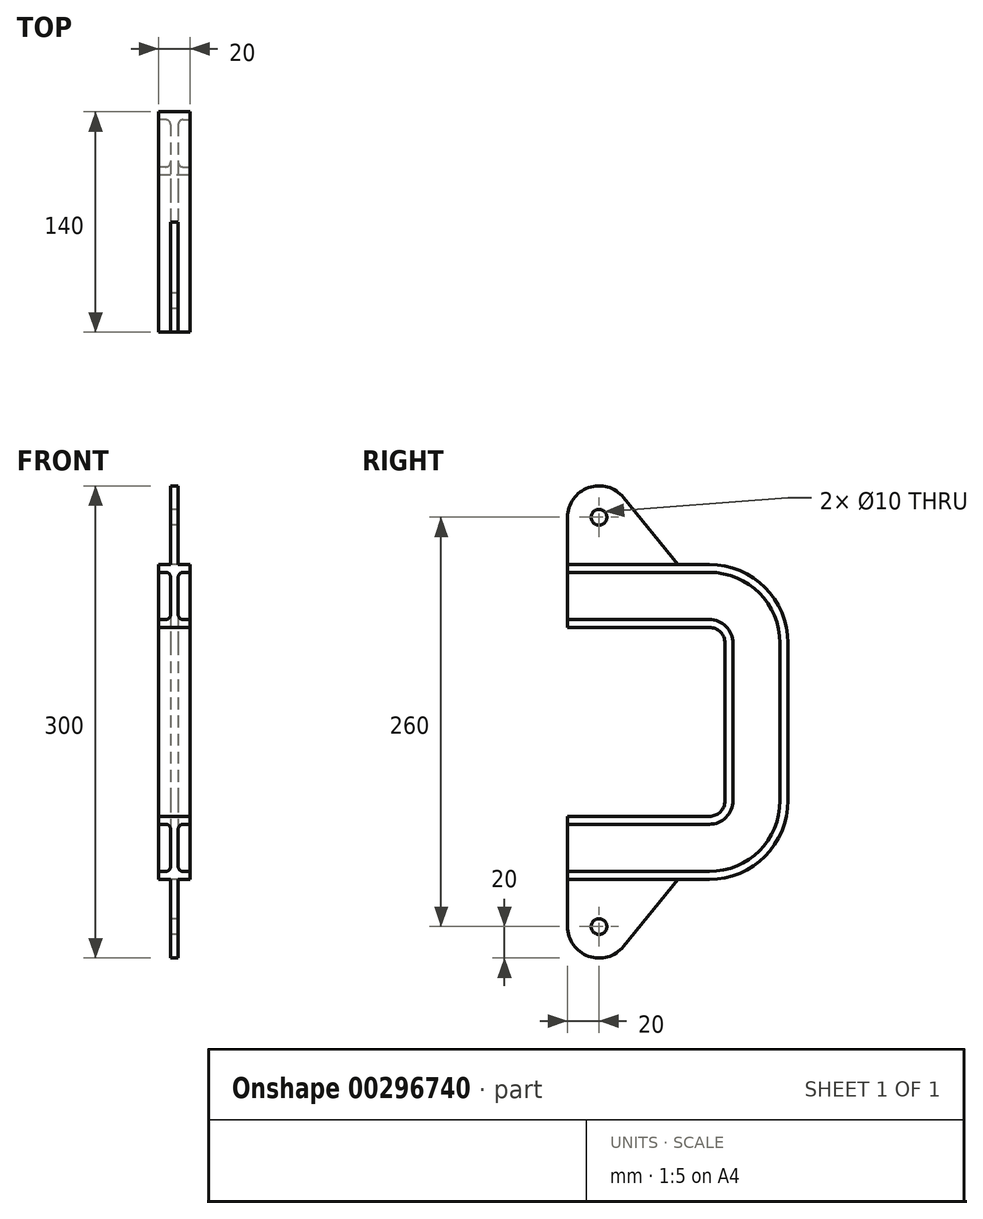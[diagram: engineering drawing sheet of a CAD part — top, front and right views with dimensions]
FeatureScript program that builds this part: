
annotation { "Feature Type Name" : "Feature", "Feature Type Description" : "" }
export const myFeature = defineFeature(function(context is Context, id is Id, definition is map)
    precondition{}
    {
        {
            var Q0;
            Q0=qCreatedBy(makeId("Front.planeOp"),FACE);
            var sketch = newSketch(context, id + "F0", { "sketchPlane" : qUnion([Q0])});
            skLineSegment(sketch, "E0", {"start": v(2.5, 0) * mm, "end": v(2.5, 12) * mm});
            skLineSegment(sketch, "E1", {"start": v(5.5, 15) * mm, "end": v(10, 15) * mm});
            skLineSegment(sketch, "E2", {"start": v(10, 15) * mm, "end": v(10, 20) * mm});
            skLineSegment(sketch, "E3", {"start": v(10, 20) * mm, "end": v(0, 20) * mm});
            skLineSegment(sketch, "E4.MirrorCS", {"start": v(-10, 15) * mm, "end": v(-10, 20) * mm});
            skLineSegment(sketch, "E5.MirrorCS", {"start": v(-5.5, 15) * mm, "end": v(-10, 15) * mm});
            skLineSegment(sketch, "E6.MirrorCS", {"start": v(-2.5, 0) * mm, "end": v(-2.5, 12) * mm});
            skLineSegment(sketch, "E7.MirrorCS", {"start": v(-10, 20) * mm, "end": v(0, 20) * mm});
            skLineSegment(sketch, "E8.MirrorCS", {"start": v(-10, -20) * mm, "end": v(0, -20) * mm});
            skLineSegment(sketch, "E9.MirrorCS", {"start": v(-2.5, 0) * mm, "end": v(-2.5, -12) * mm});
            skLineSegment(sketch, "E10.MirrorCS", {"start": v(5.5, -15) * mm, "end": v(10, -15) * mm});
            skLineSegment(sketch, "E11.MirrorCS", {"start": v(-10, -15) * mm, "end": v(-10, -20) * mm});
            skLineSegment(sketch, "E12.MirrorCS", {"start": v(2.5, 0) * mm, "end": v(2.5, -12) * mm});
            skLineSegment(sketch, "E13.MirrorCS", {"start": v(-5.5, -15) * mm, "end": v(-10, -15) * mm});
            skLineSegment(sketch, "E14.MirrorCS", {"start": v(10, -20) * mm, "end": v(0, -20) * mm});
            skLineSegment(sketch, "E15.MirrorCS", {"start": v(10, -15) * mm, "end": v(10, -20) * mm});
            skPoint(sketch, "E16.visualSharp", {"position": v(2.5, 15) * mm});
            skArc(sketch, "E16.filletArc", {"start": v(5.5, 15) * mm, "mid": v(3.38, 14.12) * mm, "end": v(2.5, 12) * mm});
            skPoint(sketch, "E17.visualSharp", {"position": v(-2.5, 15) * mm});
            skArc(sketch, "E17.filletArc", {"start": v(-2.5, 12) * mm, "mid": v(-3.38, 14.12) * mm, "end": v(-5.5, 15) * mm});
            skPoint(sketch, "E18.visualSharp", {"position": v(-2.5, -15) * mm});
            skArc(sketch, "E18.filletArc", {"start": v(-5.5, -15) * mm, "mid": v(-3.38, -14.12) * mm, "end": v(-2.5, -12) * mm});
            skPoint(sketch, "E19.visualSharp", {"position": v(2.5, -15) * mm});
            skArc(sketch, "E19.filletArc", {"start": v(2.5, -12) * mm, "mid": v(3.38, -14.12) * mm, "end": v(5.5, -15) * mm});
            skSolve(sketch);
        }
        {
            var Q0;
            Q0=qCreatedBy(makeId("Right.planeOp"),FACE);
            var sketch = newSketch(context, id + "F1", { "sketchPlane" : qUnion([Q0])});
            skLineSegment(sketch, "E20", {"start": v(0, -20) * mm, "end": v(90, -20) * mm});
            skLineSegment(sketch, "E21", {"start": v(100, -30) * mm, "end": v(100, -80) * mm});
            skPoint(sketch, "E22.visualSharp", {"position": v(100, -20) * mm});
            skArc(sketch, "E22.filletArc", {"start": v(100, -30) * mm, "mid": v(97.07, -22.93) * mm, "end": v(90, -20) * mm});
            skLineSegment(sketch, "E23", {"start": v(70.09, -80) * mm, "end": v(139.53, -80) * mm, "construction": true});
            skLineSegment(sketch, "E24.MirrorCS", {"start": v(100, -130) * mm, "end": v(100, -80) * mm});
            skLineSegment(sketch, "E25.MirrorCS", {"start": v(0, -140) * mm, "end": v(90, -140) * mm});
            skArc(sketch, "E26.MirrorCS", {"start": v(100, -130) * mm, "mid": v(97.07, -137.07) * mm, "end": v(90, -140) * mm});
            skPoint(sketch, "E27.MirrorP", {"position": v(100, -140) * mm});
            skSolve(sketch);
        }
        {
            var Q0;
            Q0=makeQuery(id+"F0.imprint","IMPRINT",FACE,{"disambiguationData":[TD([[makeQuery(id+"F0.imprint","IMPRINT",EDGE,{"derivedFrom":sQuery(id+"F0.wireOp",EDGE,"E0")}),1.0]])]});
            var Q1;
            Q1=sQuery(id+"F1.wireOp",EDGE,"E20");
            var Q2;
            Q2=sQuery(id+"F1.wireOp",EDGE,"E22.filletArc");
            var Q3;
            Q3=sQuery(id+"F1.wireOp",EDGE,"E21");
            var Q4;
            Q4=sQuery(id+"F1.wireOp",EDGE,"E24.MirrorCS");
            var Q5;
            Q5=sQuery(id+"F1.wireOp",EDGE,"E26.MirrorCS");
            var Q6;
            Q6=sQuery(id+"F1.wireOp",EDGE,"E25.MirrorCS");
            sweep(context, id + "F2", {"profiles" : qUnion([Q0]), "path" : qUnion([Q1, Q2, Q3, Q4, Q5, Q6])});
        }
        {
            var Q0;
            Q0=qCreatedBy(makeId("Right.planeOp"),FACE);
            var sketch = newSketch(context, id + "F3", { "sketchPlane" : qUnion([Q0])});
            skArc(sketch, "E28", {"start": v(140, -30) * mm, "mid": v(125.36, 5.36) * mm, "end": v(90, 20) * mm});
            skArc(sketch, "E29", {"start": v(100, -30) * mm, "mid": v(97.07, -22.93) * mm, "end": v(90, -20) * mm});
            skLineSegment(sketch, "E30", {"start": v(0, 20) * mm, "end": v(29.53, 20) * mm});
            skLineSegment(sketch, "E31", {"start": v(0, -20) * mm, "end": v(30.12, -20) * mm});
            skLineSegment(sketch, "E32", {"start": v(0, -140) * mm, "end": v(22.4, -140) * mm});
            skLineSegment(sketch, "E33", {"start": v(105, -80) * mm, "end": v(167.88, -80) * mm});
            skPoint(sketch, "E34", {"position": v(110, -10) * mm});
            skSolve(sketch);
        }
        {
            var Q0;
            Q0=qCreatedBy(makeId("Right.planeOp"),FACE);
            var sketch = newSketch(context, id + "F4", { "sketchPlane" : qUnion([Q0])});
            skLineSegment(sketch, "E35", {"start": v(0, 20) * mm, "end": v(0, 50) * mm});
            skLineSegment(sketch, "E36", {"start": v(70, 20) * mm, "end": v(35.55, 62.58) * mm});
            skArc(sketch, "E37", {"start": v(35.55, 62.58) * mm, "mid": v(13.33, 68.85) * mm, "end": v(0, 50) * mm});
            skCircle(sketch, "E38", {"center": v(20, 50) * mm, "radius": 5 * mm});
            skLineSegment(sketch, "E39", {"start": v(70, 20) * mm, "end": v(0, 20) * mm});
            skLineSegment(sketch, "E40.MirrorCS", {"start": v(70, -180) * mm, "end": v(0, -180) * mm});
            skArc(sketch, "E41.MirrorCS", {"start": v(35.55, -222.58) * mm, "mid": v(13.33, -228.85) * mm, "end": v(0, -210) * mm});
            skLineSegment(sketch, "E42.MirrorCS", {"start": v(70, -180) * mm, "end": v(35.55, -222.58) * mm});
            skLineSegment(sketch, "E43.MirrorCS", {"start": v(0, -180) * mm, "end": v(0, -210) * mm});
            skCircle(sketch, "E44.MirrorC", {"center": v(20, -210) * mm, "radius": 5 * mm});
            skSolve(sketch);
        }
        {
            var Q0;
            Q0=makeQuery(id+"F4.imprint","IMPRINT",FACE,{"disambiguationData":[TD([[makeQuery(id+"F4.imprint","IMPRINT",EDGE,{"derivedFrom":sQuery(id+"F4.wireOp",EDGE,"E35")}),-1.0]])]});
            extrude(context, id + "F5", {"entities" : qUnion([Q0]), "operationType" : NewBodyOperationType.ADD, "endBound" : BoundingType.SYMMETRIC, "depth" : 5 * mm});
        }
        {
            var Q0;
            Q0 = qSketchRegion(id + "F4", true);
            extrude(context, id + "F6", {"entities" : qUnion([Q0]), "operationType" : NewBodyOperationType.ADD, "endBound" : BoundingType.SYMMETRIC, "depth" : 5 * mm});
        }
    });
